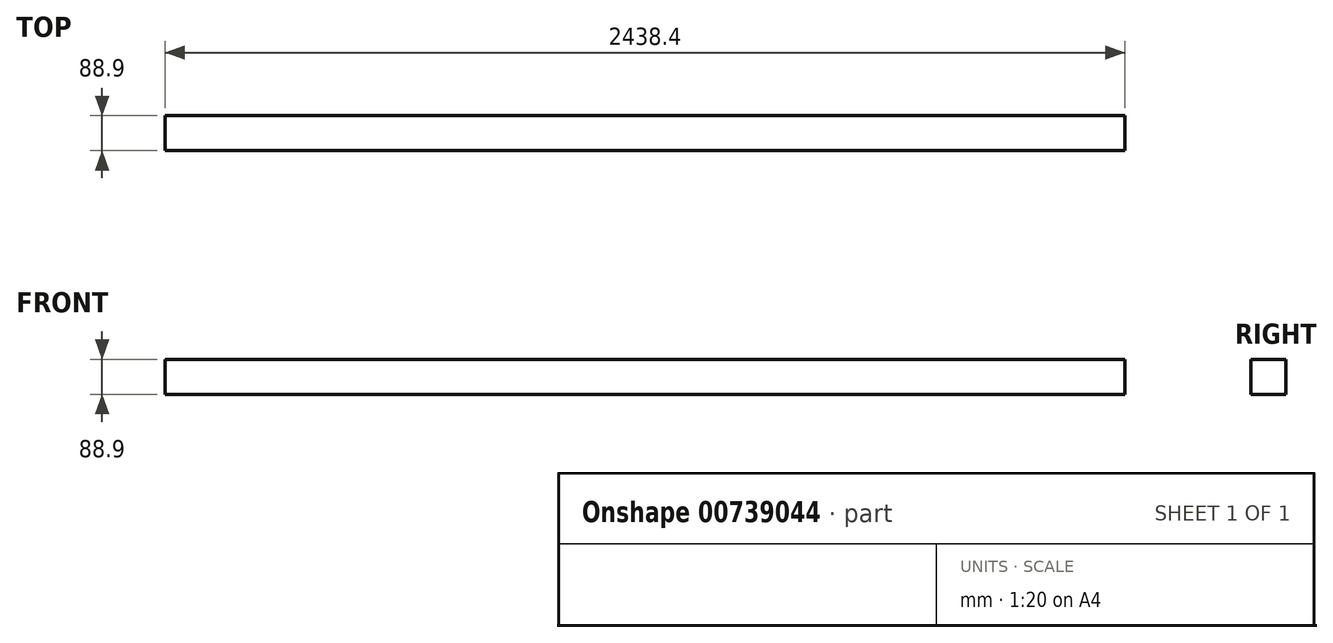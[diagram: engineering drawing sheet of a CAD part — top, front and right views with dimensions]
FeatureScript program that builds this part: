
annotation { "Feature Type Name" : "Feature", "Feature Type Description" : "" }
export const myFeature = defineFeature(function(context is Context, id is Id, definition is map)
    precondition{}
    {
        {
            var Q0;
            Q0=qCreatedBy(makeId("Front.planeOp"),FACE);
            var sketch = newSketch(context, id + "F0", { "sketchPlane" : qUnion([Q0])});
            skLineSegment(sketch, "E0.bottom", {"start": v(-109.37, 88.9) * mm, "end": v(2329.03, 88.9) * mm});
            skLineSegment(sketch, "E0.top", {"start": v(-109.37, 0) * mm, "end": v(2329.03, 0) * mm});
            skLineSegment(sketch, "E0.left", {"start": v(-109.37, 88.9) * mm, "end": v(-109.37, 0) * mm});
            skLineSegment(sketch, "E0.right", {"start": v(2329.03, 88.9) * mm, "end": v(2329.03, 0) * mm});
            skSolve(sketch);
        }
        {
            var Q0;
            Q0 = qSketchRegion(id + "F0", true);
            extrude(context, id + "F1", {"entities" : qUnion([Q0]), "depth" : 88.9 * mm, "offsetDistance" : 25.4 * mm});
        }
    });
